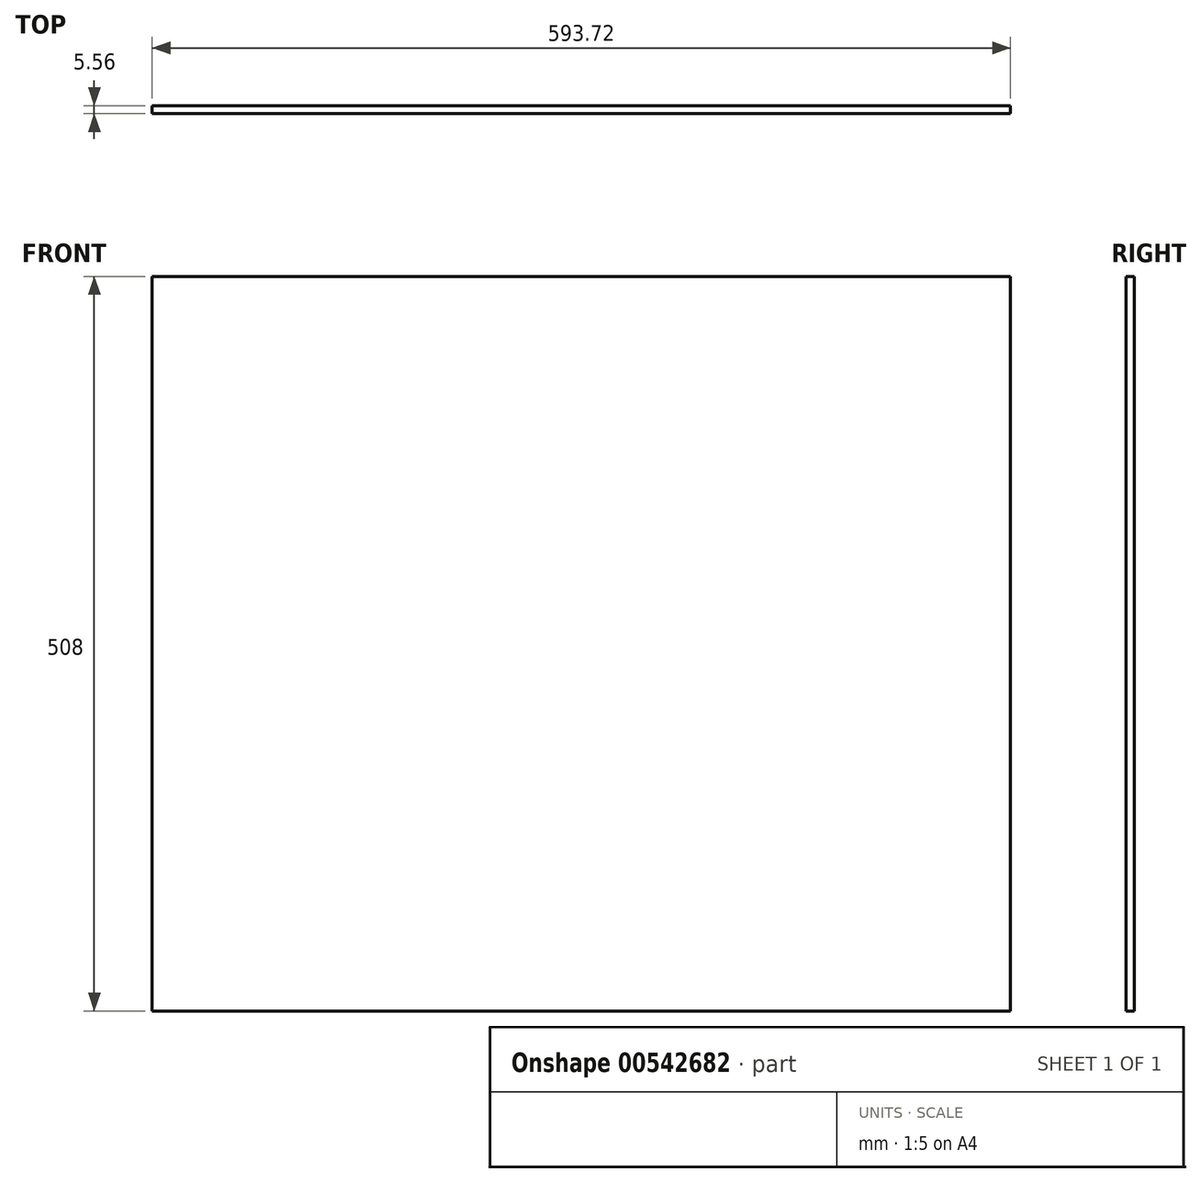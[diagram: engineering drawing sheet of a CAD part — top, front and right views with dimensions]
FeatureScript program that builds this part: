
annotation { "Feature Type Name" : "Feature", "Feature Type Description" : "" }
export const myFeature = defineFeature(function(context is Context, id is Id, definition is map)
    precondition{}
    {
        {
            var Q0;
            Q0=qCreatedBy(makeId("Front.planeOp"),FACE);
            var sketch = newSketch(context, id + "F0", { "sketchPlane" : qUnion([Q0])});
            skLineSegment(sketch, "E0.bottom", {"start": v(-296.86, 254) * mm, "end": v(296.86, 254) * mm});
            skLineSegment(sketch, "E0.top", {"start": v(-296.86, -254) * mm, "end": v(296.86, -254) * mm});
            skLineSegment(sketch, "E0.left", {"start": v(-296.86, 254) * mm, "end": v(-296.86, -254) * mm});
            skLineSegment(sketch, "E0.right", {"start": v(296.86, 254) * mm, "end": v(296.86, -254) * mm});
            skLineSegment(sketch, "E1", {"start": v(0, 254) * mm, "end": v(0, -254) * mm, "construction": true});
            skSolve(sketch);
        }
        {
            var Q0;
            Q0=makeQuery(id+"F0.imprint","IMPRINT",FACE,{"disambiguationData":[TD([[makeQuery(id+"F0.imprint","IMPRINT",EDGE,{"derivedFrom":sQuery(id+"F0.wireOp",EDGE,"E0.bottom")}),-1.0]])]});
            extrude(context, id + "F1", {"entities" : qUnion([Q0]), "depth" : 5.56 * mm, "offsetDistance" : 25.4 * mm});
        }
    });
